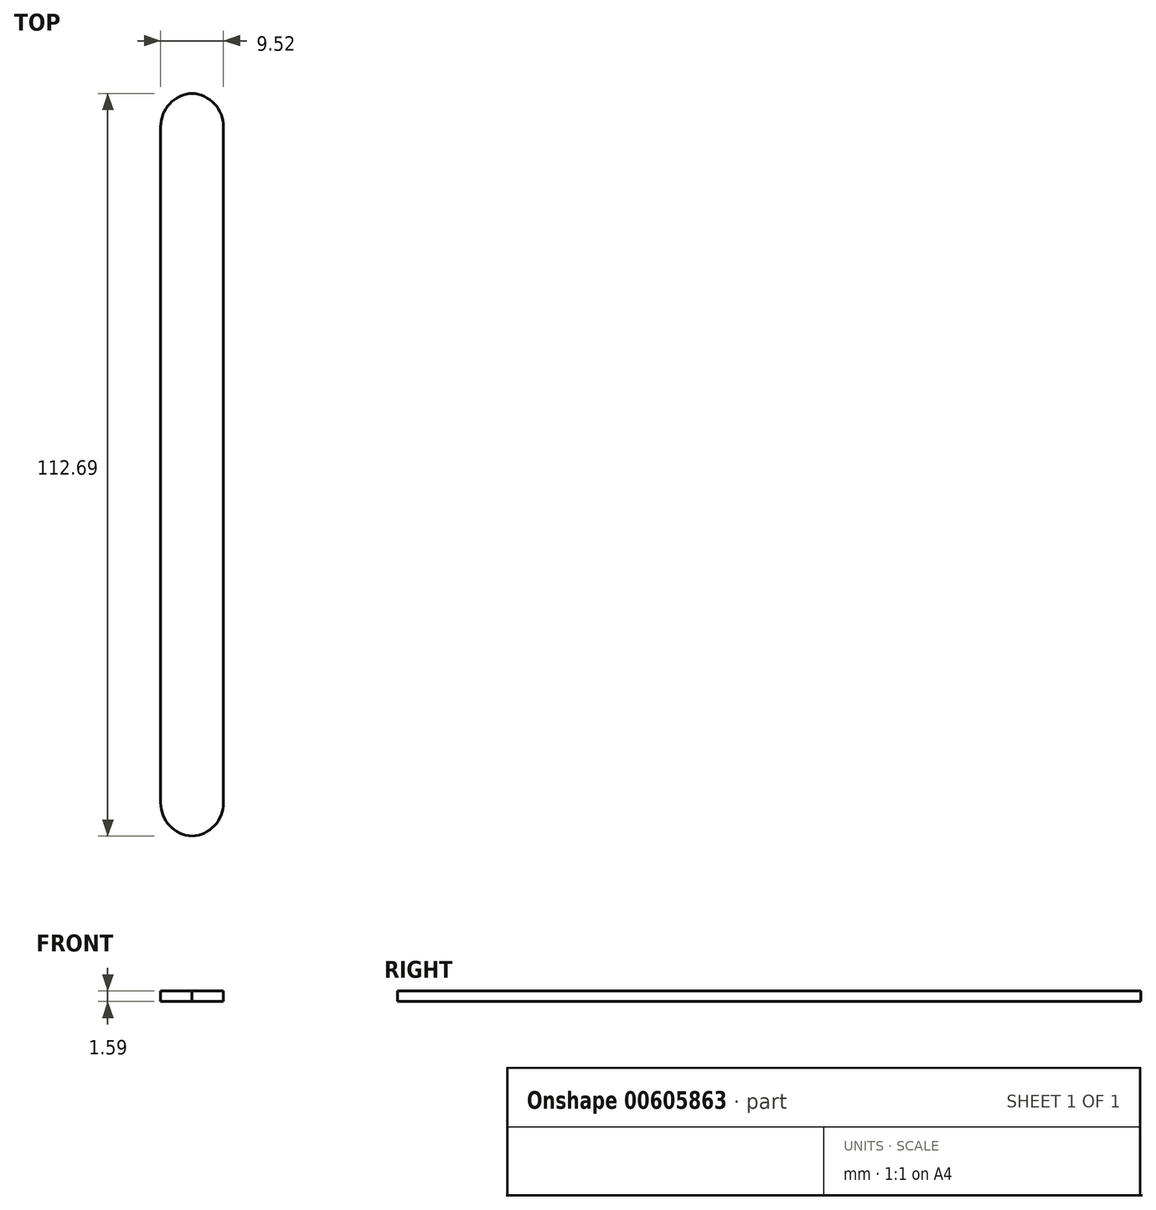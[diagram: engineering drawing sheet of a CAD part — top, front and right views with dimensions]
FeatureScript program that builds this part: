
annotation { "Feature Type Name" : "Feature", "Feature Type Description" : "" }
export const myFeature = defineFeature(function(context is Context, id is Id, definition is map)
    precondition{}
    {
        {
            var Q0;
            Q0=qCreatedBy(makeId("Top.planeOp"),FACE);
            var sketch = newSketch(context, id + "F0", { "sketchPlane" : qUnion([Q0])});
            skLineSegment(sketch, "E0", {"start": v(-4.76, 112.71) * mm, "end": v(-4.76, 0) * mm});
            skLineSegment(sketch, "E1", {"start": v(-4.76, 0) * mm, "end": v(4.76, 0) * mm});
            skLineSegment(sketch, "E2", {"start": v(4.76, 0) * mm, "end": v(4.76, 112.71) * mm});
            skLineSegment(sketch, "E3", {"start": v(-4.76, 112.71) * mm, "end": v(4.76, 112.71) * mm});
            skLineSegment(sketch, "E4.right", {"start": v(4.76, 112.71) * mm, "end": v(4.76, 0) * mm});
            skSolve(sketch);
        }
        {
            var Q0;
            Q0=makeQuery(id+"F0.imprint","IMPRINT",FACE,{"disambiguationData":[TD([[makeQuery(id+"F0.imprint","IMPRINT",EDGE,{"derivedFrom":sQuery(id+"F0.wireOp",EDGE,"E1")}),1.0]])]});
            extrude(context, id + "F1", {"entities" : qUnion([Q0]), "depth" : 1.59 * mm, "offsetDistance" : 25.4 * mm});
        }
        {
            var Q0;
            Q0=makeQuery(id+"F1.opExtrude","SWEPT_EDGE",EDGE,{"disambiguationData":[OSD([sQuery(id+"F0.wireOp",EDGE,"E1"),sQuery(id+"F0.wireOp",EDGE,"E4.right")])]});
            var Q1;
            Q1=makeQuery(id+"F1.opExtrude","SWEPT_EDGE",EDGE,{"disambiguationData":[OSD([sQuery(id+"F0.wireOp",EDGE,"E1"),sQuery(id+"F0.wireOp",EDGE,"E0")])]});
            var Q2;
            Q2=makeQuery(id+"F1.opExtrude","SWEPT_EDGE",EDGE,{"disambiguationData":[OSD([sQuery(id+"F0.wireOp",EDGE,"E3"),sQuery(id+"F0.wireOp",EDGE,"E4.right")])]});
            var Q3;
            Q3=makeQuery(id+"F1.opExtrude","SWEPT_EDGE",EDGE,{"disambiguationData":[OSD([sQuery(id+"F0.wireOp",EDGE,"E3"),sQuery(id+"F0.wireOp",EDGE,"E0")])]});
            fillet(context, id + "F2", {"entities" : qUnion([Q0, Q1, Q2, Q3]), "radius" : 5.08 * mm, "tangentPropagation" : true, "allowEdgeOverflow" : false});
        }
    });
